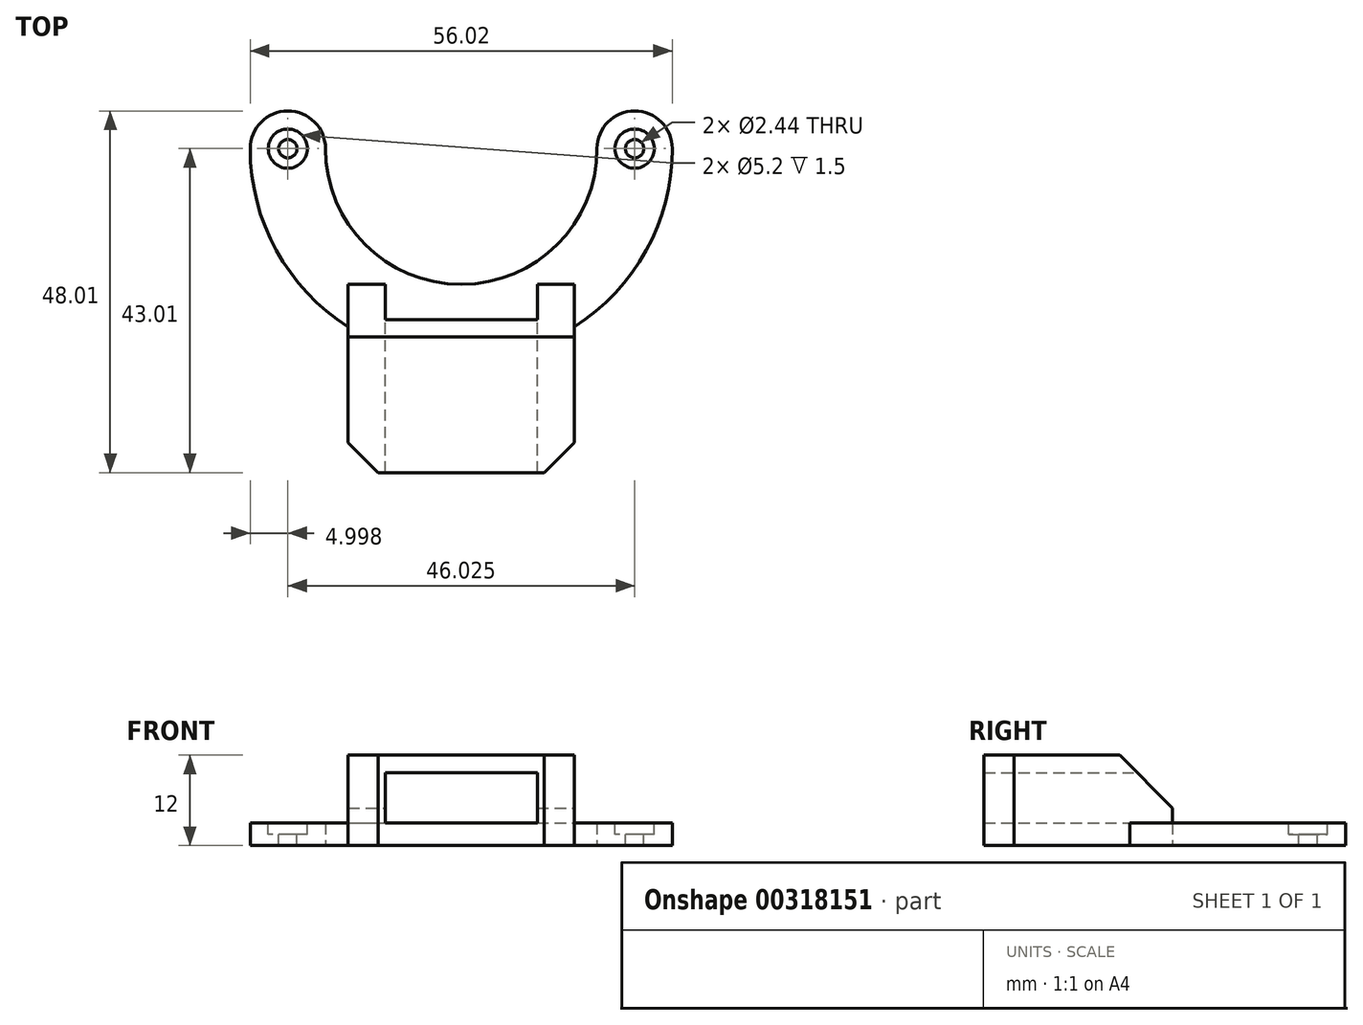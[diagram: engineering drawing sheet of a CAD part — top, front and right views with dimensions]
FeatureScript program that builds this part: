
annotation { "Feature Type Name" : "Feature", "Feature Type Description" : "" }
export const myFeature = defineFeature(function(context is Context, id is Id, definition is map)
    precondition{}
    {
        {
            var Q0;
            Q0=qCreatedBy(makeId("Top.planeOp"),FACE);
            var sketch = newSketch(context, id + "F0", { "sketchPlane" : qUnion([Q0])});
            skCircle(sketch, "E0", {"center": v(0, 0) * mm, "radius": 23.01 * mm, "construction": true});
            skArc(sketch, "E1", {"start": v(-18.01, 0) * mm, "mid": v(0, -18.01) * mm, "end": v(18.01, 0) * mm});
            skArc(sketch, "E2", {"start": v(-28.01, 0) * mm, "mid": v(0, -28.01) * mm, "end": v(28.01, 0) * mm});
            skLineSegment(sketch, "E3", {"start": v(-28.01, 0) * mm, "end": v(-18.01, 0) * mm, "construction": true});
            skLineSegment(sketch, "E4", {"start": v(18.01, 0) * mm, "end": v(28.01, 0) * mm, "construction": true});
            skLineSegment(sketch, "E5", {"start": v(-28.01, 0) * mm, "end": v(-28.01, 5) * mm});
            skLineSegment(sketch, "E6", {"start": v(-28.01, 5) * mm, "end": v(-18.01, 5) * mm});
            skLineSegment(sketch, "E7", {"start": v(-18.01, 5) * mm, "end": v(-18.01, 0) * mm});
            skLineSegment(sketch, "E8", {"start": v(18.01, 0) * mm, "end": v(18.01, 5) * mm});
            skLineSegment(sketch, "E9", {"start": v(18.01, 5) * mm, "end": v(28.01, 5) * mm});
            skLineSegment(sketch, "E10", {"start": v(28.01, 5) * mm, "end": v(28.01, 0) * mm});
            skSolve(sketch);
        }
        {
            var Q0;
            Q0 = qSketchRegion(id + "F0", true);
            extrude(context, id + "F1", {"entities" : qUnion([Q0]), "depth" : 3 * mm});
        }
        {
            var Q0;
            Q0=makeQuery(id+"F1.opExtrude","SWEPT_EDGE",EDGE,{"disambiguationData":[OSD([sQuery(id+"F0.wireOp",EDGE,"E5"),sQuery(id+"F0.wireOp",EDGE,"E6")])]});
            var Q1;
            Q1=makeQuery(id+"F1.opExtrude","SWEPT_EDGE",EDGE,{"disambiguationData":[OSD([sQuery(id+"F0.wireOp",EDGE,"E6"),sQuery(id+"F0.wireOp",EDGE,"E7")])]});
            var Q2;
            Q2=makeQuery(id+"F1.opExtrude","SWEPT_EDGE",EDGE,{"disambiguationData":[OSD([sQuery(id+"F0.wireOp",EDGE,"E8"),sQuery(id+"F0.wireOp",EDGE,"E9")])]});
            var Q3;
            Q3=makeQuery(id+"F1.opExtrude","SWEPT_EDGE",EDGE,{"disambiguationData":[OSD([sQuery(id+"F0.wireOp",EDGE,"E9"),sQuery(id+"F0.wireOp",EDGE,"E10")])]});
            fillet(context, id + "F2", {"entities" : qUnion([Q0, Q1, Q2, Q3]), "radius" : 5 * mm, "tangentPropagation" : true, "allowEdgeOverflow" : false});
        }
        {
            var Q0;
            Q0=makeQuery(id+"F1.opExtrude","CAP_FACE",FACE,{"disambiguationData":[OSD([sQuery(id+"F0.wireOp",EDGE,"E1"),sQuery(id+"F0.wireOp",EDGE,"E2"),sQuery(id+"F0.wireOp",EDGE,"E5"),sQuery(id+"F0.wireOp",EDGE,"E6"),sQuery(id+"F0.wireOp",EDGE,"E7"),sQuery(id+"F0.wireOp",EDGE,"E8"),sQuery(id+"F0.wireOp",EDGE,"E9"),sQuery(id+"F0.wireOp",EDGE,"E10")])],"isStart":false});
            var sketch = newSketch(context, id + "F3", { "sketchPlane" : qUnion([Q0])});
            skPoint(sketch, "E11", {"position": v(-23.01, 0) * mm});
            skPoint(sketch, "E12", {"position": v(23.01, 0) * mm});
            skSolve(sketch);
        }
        {
            var Q0;
            Q0=sQuery(id+"F3.wireOp",VERTEX,"E11");
            var Q1;
            Q1=sQuery(id+"F3.wireOp",VERTEX,"E12");
            var Q2;
            Q2=makeQuery(id+"F1.opExtrude","SWEPT_BODY",BODY,{"disambiguationData":[OSD([sQuery(id+"F0.wireOp",EDGE,"E1"),sQuery(id+"F0.wireOp",EDGE,"E2"),sQuery(id+"F0.wireOp",EDGE,"E5"),sQuery(id+"F0.wireOp",EDGE,"E6"),sQuery(id+"F0.wireOp",EDGE,"E7"),sQuery(id+"F0.wireOp",EDGE,"E8"),sQuery(id+"F0.wireOp",EDGE,"E9"),sQuery(id+"F0.wireOp",EDGE,"E10")])]});
            hole(context, id + "F4", {"style" : HoleStyle.C_BORE, "endStyle" : HoleEndStyle.THROUGH, "holeDiameter" : 2.44 * mm, "cBoreDiameter" : 5.2 * mm, "cBoreDepth" : 1.5 * mm, "tappedDepth" : 12 * mm, "tapClearance" : 3, "locations" : qUnion([Q0, Q1]), "scope" : qUnion([Q2])});
        }
        {
            var Q0;
            Q0=qCreatedBy(makeId("Top.planeOp"),FACE);
            var sketch = newSketch(context, id + "F5", { "sketchPlane" : qUnion([Q0])});
            skLineSegment(sketch, "E13.bottom", {"start": v(15, -18.01) * mm, "end": v(-15, -18.01) * mm});
            skLineSegment(sketch, "E13.top", {"start": v(15, -43.01) * mm, "end": v(-15, -43.01) * mm});
            skLineSegment(sketch, "E13.left", {"start": v(15, -18.01) * mm, "end": v(15, -43.01) * mm});
            skLineSegment(sketch, "E13.right", {"start": v(-15, -18.01) * mm, "end": v(-15, -43.01) * mm});
            skPoint(sketch, "E13.middle", {"position": v(0, -30.51) * mm});
            skSolve(sketch);
        }
        {
            var Q0;
            Q0=makeQuery(id+"F5.imprint","IMPRINT",FACE,{"disambiguationData":[TD([[makeQuery(id+"F5.imprint","IMPRINT",EDGE,{"derivedFrom":sQuery(id+"F5.wireOp",EDGE,"E13.bottom")}),1.0]])]});
            extrude(context, id + "F6", {"entities" : qUnion([Q0]), "operationType" : NewBodyOperationType.ADD, "depth" : 12 * mm});
        }
        {
            var Q0;
            Q0=makeQuery(id+"F6.opExtrude","SWEPT_FACE",FACE,{"disambiguationData":[OSD([sQuery(id+"F5.wireOp",EDGE,"E13.bottom")])]});
            var sketch = newSketch(context, id + "F7", { "sketchPlane" : qUnion([Q0])});
            skLineSegment(sketch, "E14.bottom", {"start": v(10.1, 3) * mm, "end": v(-10.1, 3) * mm});
            skLineSegment(sketch, "E14.top", {"start": v(10.1, 9.7) * mm, "end": v(-10.1, 9.7) * mm});
            skLineSegment(sketch, "E14.left", {"start": v(10.1, 3) * mm, "end": v(10.1, 9.7) * mm});
            skLineSegment(sketch, "E14.right", {"start": v(-10.1, 3) * mm, "end": v(-10.1, 9.7) * mm});
            skPoint(sketch, "E14.middle", {"position": v(0, 6.35) * mm});
            skSolve(sketch);
        }
        {
            var Q0;
            Q0=makeQuery(id+"F7.imprint","IMPRINT",FACE,{"disambiguationData":[TD([[makeQuery(id+"F7.imprint","IMPRINT",EDGE,{"derivedFrom":sQuery(id+"F7.wireOp",EDGE,"E14.top")}),1.0]])]});
            extrude(context, id + "F8", {"entities" : qUnion([Q0]), "operationType" : NewBodyOperationType.REMOVE, "endBound" : BoundingType.THROUGH_ALL, "oppositeDirection" : true, "depth" : 25 * mm});
        }
        {
            var Q0;
            Q0=makeQuery(id+"F6.opExtrude","CAP_EDGE",EDGE,{"disambiguationData":[OSD([sQuery(id+"F5.wireOp",EDGE,"E13.bottom")])],"isStart":false});
            chamfer(context, id + "F9", {"entities" : qUnion([Q0]), "width" : 7 * mm, "tangentPropagation" : true});
        }
        {
            var Q0;
            Q0=makeQuery(id+"F6.opExtrude","SWEPT_EDGE",EDGE,{"disambiguationData":[OSD([sQuery(id+"F5.wireOp",EDGE,"E13.top"),sQuery(id+"F5.wireOp",EDGE,"E13.right")])]});
            var Q1;
            Q1=makeQuery(id+"F6.opExtrude","SWEPT_EDGE",EDGE,{"disambiguationData":[OSD([sQuery(id+"F5.wireOp",EDGE,"E13.top"),sQuery(id+"F5.wireOp",EDGE,"E13.left")])]});
            chamfer(context, id + "F10", {"entities" : qUnion([Q0, Q1]), "width" : 4 * mm, "tangentPropagation" : true});
        }
    });
